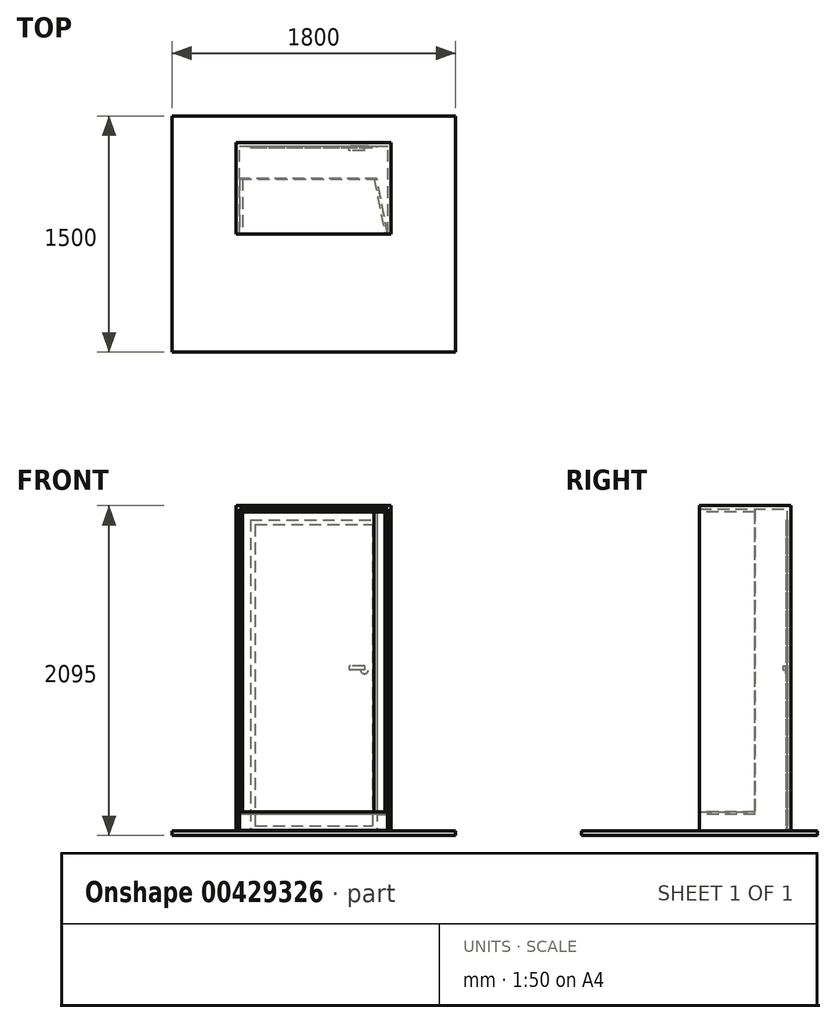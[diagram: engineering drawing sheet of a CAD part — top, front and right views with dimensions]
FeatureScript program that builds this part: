
annotation { "Feature Type Name" : "Feature", "Feature Type Description" : "" }
export const myFeature = defineFeature(function(context is Context, id is Id, definition is map)
    precondition{}
    {
        {
            var Q0;
            Q0=qCreatedBy(makeId("Front.planeOp"),FACE);
            var sketch = newSketch(context, id + "F0", { "sketchPlane" : qUnion([Q0])});
            skLineSegment(sketch, "E0.bottom", {"start": v(-472.5, -1022.5) * mm, "end": v(472.5, -1022.5) * mm});
            skLineSegment(sketch, "E0.top", {"start": v(-472.5, 1022.5) * mm, "end": v(472.5, 1022.5) * mm});
            skLineSegment(sketch, "E0.left", {"start": v(-472.5, -1022.5) * mm, "end": v(-472.5, 1022.5) * mm});
            skLineSegment(sketch, "E0.right", {"start": v(472.5, -1022.5) * mm, "end": v(472.5, 1022.5) * mm});
            skPoint(sketch, "E0.middle", {"position": v(0, 0) * mm});
            skLineSegment(sketch, "E1.0", {"start": v(492.5, -1022.5) * mm, "end": v(492.5, 1042.5) * mm});
            skLineSegment(sketch, "E1.1", {"start": v(-492.5, 1042.5) * mm, "end": v(492.5, 1042.5) * mm});
            skLineSegment(sketch, "E1.2", {"start": v(-492.5, -1022.5) * mm, "end": v(-492.5, 1042.5) * mm});
            skLineSegment(sketch, "E2", {"start": v(-492.5, -1022.5) * mm, "end": v(-472.5, -1022.5) * mm});
            skLineSegment(sketch, "E3", {"start": v(472.5, -1022.5) * mm, "end": v(492.5, -1022.5) * mm});
            skSolve(sketch);
        }
        {
            var Q0;
            Q0=makeQuery(id+"F0.imprint","IMPRINT",FACE,{"disambiguationData":[TD([[makeQuery(id+"F0.imprint","IMPRINT",EDGE,{"derivedFrom":sQuery(id+"F0.wireOp",EDGE,"E0.top")}),1.0]])]});
            extrude(context, id + "F1", {"entities" : qUnion([Q0]), "depth" : 580 * mm});
        }
        {
            var Q0;
            Q0=qCreatedBy(makeId("Front.planeOp"),FACE);
            var sketch = newSketch(context, id + "F2", { "sketchPlane" : qUnion([Q0])});
            skLineSegment(sketch, "E4.bottom", {"start": v(-372.5, 922.5) * mm, "end": v(372.5, 922.5) * mm});
            skLineSegment(sketch, "E4.top", {"start": v(-372.5, -992.5) * mm, "end": v(372.5, -992.5) * mm});
            skLineSegment(sketch, "E4.left", {"start": v(-372.5, 922.5) * mm, "end": v(-372.5, -992.5) * mm});
            skLineSegment(sketch, "E4.right", {"start": v(372.5, 922.5) * mm, "end": v(372.5, -992.5) * mm});
            skLineSegment(sketch, "E5.0", {"start": v(-402.5, 952.5) * mm, "end": v(-402.5, -1022.5) * mm});
            skLineSegment(sketch, "E5.1", {"start": v(-402.5, 952.5) * mm, "end": v(402.5, 952.5) * mm});
            skLineSegment(sketch, "E5.2", {"start": v(402.5, 952.5) * mm, "end": v(402.5, -1022.5) * mm});
            skLineSegment(sketch, "E5.3", {"start": v(-402.5, -1022.5) * mm, "end": v(402.5, -1022.5) * mm});
            skCircle(sketch, "E6", {"center": v(322.5, 0) * mm, "radius": 25 * mm});
            skLineSegment(sketch, "E7.bottom", {"start": v(322.5, 25) * mm, "end": v(232.5, 25) * mm});
            skLineSegment(sketch, "E7.top", {"start": v(322.5, 0) * mm, "end": v(232.5, 0) * mm});
            skLineSegment(sketch, "E7.left", {"start": v(322.5, 25) * mm, "end": v(322.5, 0) * mm});
            skLineSegment(sketch, "E7.right", {"start": v(222.5, 15) * mm, "end": v(222.5, 10) * mm});
            skPoint(sketch, "E8.visualSharp", {"position": v(222.5, 25) * mm});
            skArc(sketch, "E8.filletArc", {"start": v(232.5, 25) * mm, "mid": v(225.43, 22.07) * mm, "end": v(222.5, 15) * mm});
            skPoint(sketch, "E9.visualSharp", {"position": v(222.5, 0) * mm});
            skArc(sketch, "E9.filletArc", {"start": v(222.5, 10) * mm, "mid": v(225.43, 2.93) * mm, "end": v(232.5, 0) * mm});
            skLineSegment(sketch, "E10", {"start": v(-472.5, -1022.5) * mm, "end": v(-402.5, -1022.5) * mm});
            skLineSegment(sketch, "E11", {"start": v(402.5, -1022.5) * mm, "end": v(472.5, -1022.5) * mm});
            skLineSegment(sketch, "E12.bottom", {"start": v(-472.5, -1022.5) * mm, "end": v(472.5, -1022.5) * mm});
            skLineSegment(sketch, "E12.top", {"start": v(-472.5, 1022.5) * mm, "end": v(472.5, 1022.5) * mm});
            skLineSegment(sketch, "E12.left", {"start": v(-472.5, -1022.5) * mm, "end": v(-472.5, 1022.5) * mm});
            skLineSegment(sketch, "E12.right", {"start": v(472.5, -1022.5) * mm, "end": v(472.5, 1022.5) * mm});
            skSolve(sketch);
        }
        {
            var Q0;
            {var subQ1=sQuery(id+"F2.wireOp",EDGE,"E5.0");Q0=makeQuery(id+"F2.imprint","IMPRINT",FACE,{"disambiguationData":[TD([[makeQuery(id+"F2.imprint","IMPRINT",EDGE,{"derivedFrom":subQ1}),-1.0]])]});}
            var Q1;
            Q1=makeQuery(id+"F2.imprint","IMPRINT",FACE,{"disambiguationData":[TD([[makeQuery(id+"F2.imprint","IMPRINT",EDGE,{"derivedFrom":sQuery(id+"F2.wireOp",EDGE,"E4.bottom")}),-1.0]])]});
            extrude(context, id + "F3", {"entities" : qUnion([Q0, Q1]), "depth" : 20 * mm});
        }
        {
            var Q0;
            Q0=makeQuery(id+"F2.imprint","IMPRINT",FACE,{"disambiguationData":[TD([[makeQuery(id+"F2.imprint","IMPRINT",EDGE,{"derivedFrom":sQuery(id+"F2.wireOp",EDGE,"E4.bottom")}),1.0]])]});
            extrude(context, id + "F4", {"entities" : qUnion([Q0]), "operationType" : NewBodyOperationType.ADD, "depth" : 30 * mm});
        }
        {
            var Q0;
            {var subQ0=sQuery(id+"F2.wireOp",EDGE,"E7.left");Q0=makeQuery(id+"F2.imprint","IMPRINT",FACE,{"disambiguationData":[TD([[makeQuery(id+"F2.imprint","IMPRINT",EDGE,{"derivedFrom":subQ0}),1.0]])]});}
            extrude(context, id + "F5", {"entities" : qUnion([Q0]), "operationType" : NewBodyOperationType.ADD, "depth" : 30 * mm});
        }
        {
            var Q0;
            {var subQ4=sQuery(id+"F2.wireOp",EDGE,"E7.bottom");Q0=makeQuery(id+"F2.imprint","IMPRINT",FACE,{"disambiguationData":[TD([[makeQuery(id+"F2.imprint","IMPRINT",EDGE,{"derivedFrom":subQ4}),1.0]])]});}
            var Q1;
            {var subQ0=sQuery(id+"F2.wireOp",EDGE,"E7.left");Q1=makeQuery(id+"F2.imprint","IMPRINT",FACE,{"disambiguationData":[TD([[makeQuery(id+"F2.imprint","IMPRINT",EDGE,{"derivedFrom":subQ0}),-1.0]])]});}
            extrude(context, id + "F6", {"entities" : qUnion([Q0, Q1]), "operationType" : NewBodyOperationType.ADD, "depth" : 50 * mm});
        }
        {
            var Q0;
            Q0=makeQuery(id+"F1.opExtrude","SWEPT_FACE",FACE,{"disambiguationData":[OSD([sQuery(id+"F0.wireOp",EDGE,"E2")])]});
            var sketch = newSketch(context, id + "F7", { "sketchPlane" : qUnion([Q0])});
            skLineSegment(sketch, "E13.bottom", {"start": v(-900, -170) * mm, "end": v(900, -170) * mm});
            skLineSegment(sketch, "E13.top", {"start": v(-900, 1330) * mm, "end": v(900, 1330) * mm});
            skLineSegment(sketch, "E13.left", {"start": v(-900, -170) * mm, "end": v(-900, 1330) * mm});
            skLineSegment(sketch, "E13.right", {"start": v(900, -170) * mm, "end": v(900, 1330) * mm});
            skPoint(sketch, "E13.middle", {"position": v(0, 580) * mm});
            skSolve(sketch);
        }
        {
            var Q0;
            Q0 = qSketchRegion(id + "F7", true);
            extrude(context, id + "F8", {"entities" : qUnion([Q0]), "operationType" : NewBodyOperationType.ADD, "depth" : 30 * mm});
        }
        {
            var Q0;
            Q0=makeQuery(id+"F1.opExtrude","CAP_FACE",FACE,{"disambiguationData":[OSD([sQuery(id+"F0.wireOp",EDGE,"E0.top"),sQuery(id+"F0.wireOp",EDGE,"E0.left"),sQuery(id+"F0.wireOp",EDGE,"E0.right"),sQuery(id+"F0.wireOp",EDGE,"E1.0"),sQuery(id+"F0.wireOp",EDGE,"E1.1"),sQuery(id+"F0.wireOp",EDGE,"E1.2"),sQuery(id+"F0.wireOp",EDGE,"E2"),sQuery(id+"F0.wireOp",EDGE,"E3")])],"isStart":false});
            var sketch = newSketch(context, id + "F9", { "sketchPlane" : qUnion([Q0])});
            skLineSegment(sketch, "E14.bottom", {"start": v(-472.5, 1022.5) * mm, "end": v(472.5, 1022.5) * mm, "construction": true});
            skLineSegment(sketch, "E14.top", {"start": v(-472.5, -1022.5) * mm, "end": v(472.5, -1022.5) * mm, "construction": true});
            skLineSegment(sketch, "E14.left", {"start": v(-472.5, 1022.5) * mm, "end": v(-472.5, -1022.5) * mm, "construction": true});
            skLineSegment(sketch, "E14.right", {"start": v(472.5, 1022.5) * mm, "end": v(472.5, -1022.5) * mm, "construction": true});
            skLineSegment(sketch, "E15.0", {"start": v(470, 1020) * mm, "end": v(470, -1020) * mm});
            skLineSegment(sketch, "E15.1", {"start": v(-470, 1020) * mm, "end": v(470, 1020) * mm});
            skLineSegment(sketch, "E15.2", {"start": v(-470, 1020) * mm, "end": v(-470, -1020) * mm});
            skLineSegment(sketch, "E15.3", {"start": v(-470, -1020) * mm, "end": v(470, -1020) * mm});
            skLineSegment(sketch, "E16.0", {"start": v(-452, 1002) * mm, "end": v(-452, -902) * mm});
            skLineSegment(sketch, "E16.1", {"start": v(-452, 1002) * mm, "end": v(452, 1002) * mm});
            skLineSegment(sketch, "E16.2", {"start": v(452, 1002) * mm, "end": v(452, -902) * mm});
            skLineSegment(sketch, "E17", {"start": v(-452, -920) * mm, "end": v(452, -920) * mm});
            skLineSegment(sketch, "E18", {"start": v(-452, -920) * mm, "end": v(-470, -920) * mm});
            skLineSegment(sketch, "E19", {"start": v(452, -920) * mm, "end": v(470, -920) * mm});
            skLineSegment(sketch, "E20", {"start": v(-452, 1002) * mm, "end": v(-470, 1002) * mm});
            skLineSegment(sketch, "E21", {"start": v(452, 1002) * mm, "end": v(470, 1002) * mm});
            skLineSegment(sketch, "E22.0", {"start": v(-470, -902) * mm, "end": v(470, -902) * mm});
            skSolve(sketch);
        }
        {
            var Q0;
            Q0=makeQuery(id+"F9.imprint","IMPRINT",FACE,{"disambiguationData":[TD([[makeQuery(id+"F9.imprint","IMPRINT",EDGE,{"derivedFrom":sQuery(id+"F9.wireOp",EDGE,"E16.0")}),-1.0]])]});
            extrude(context, id + "F10", {"entities" : qUnion([Q0]), "oppositeDirection" : true, "depth" : 350 * mm});
        }
        {
            var Q0;
            {var subQ1=sQuery(id+"F9.wireOp",EDGE,"E15.1");Q0=makeQuery(id+"F9.imprint","IMPRINT",FACE,{"disambiguationData":[TD([[makeQuery(id+"F9.imprint","IMPRINT",EDGE,{"derivedFrom":subQ1}),-1.0]])]});}
            extrude(context, id + "F11", {"entities" : qUnion([Q0]), "oppositeDirection" : true, "depth" : 350 * mm});
        }
        {
            var Q0;
            Q0=makeQuery(id+"F9.imprint","IMPRINT",FACE,{"disambiguationData":[TD([[makeQuery(id+"F9.imprint","IMPRINT",EDGE,{"derivedFrom":sQuery(id+"F9.wireOp",EDGE,"E17")}),1.0]])]});
            extrude(context, id + "F12", {"entities" : qUnion([Q0]), "oppositeDirection" : true, "depth" : 353 * mm, "hasSecondDirection" : true, "secondDirectionOppositeDirection" : true, "secondDirectionDepth" : 3 * mm});
        }
        {
            var Q0;
            Q0=makeQuery(id+"F9.imprint","IMPRINT",FACE,{"disambiguationData":[TD([[makeQuery(id+"F9.imprint","IMPRINT",EDGE,{"derivedFrom":sQuery(id+"F9.wireOp",EDGE,"E17")}),1.0]])]});
            var Q1;
            {var subQ0=sQuery(id+"F9.wireOp",EDGE,"E15.3");Q1=makeQuery(id+"F9.imprint","IMPRINT",FACE,{"disambiguationData":[TD([[makeQuery(id+"F9.imprint","IMPRINT",EDGE,{"derivedFrom":subQ0}),1.0]])]});}
            extrude(context, id + "F13", {"entities" : qUnion([Q0, Q1]), "oppositeDirection" : true, "depth" : 3 * mm});
        }
        {
            var Q0;
            Q0=makeQuery(id+"F12.opExtrude","SWEPT_FACE",FACE,{"disambiguationData":[OSD([sQuery(id+"F9.wireOp",EDGE,"E22.0")])]});
            var sketch = newSketch(context, id + "F14", { "sketchPlane" : qUnion([Q0])});
            skCircle(sketch, "E23", {"center": v(-470, -580) * mm, "radius": 940 * mm});
            skLineSegment(sketch, "E24", {"start": v(401.2, -227) * mm, "end": v(470, -580) * mm});
            skLineSegment(sketch, "E25", {"start": v(383.2, -227) * mm, "end": v(452, -580) * mm});
            skLineSegment(sketch, "E26", {"start": v(452, -580) * mm, "end": v(470, -580) * mm});
            skLineSegment(sketch, "E27", {"start": v(401.2, -227) * mm, "end": v(383.2, -227) * mm});
            skLineSegment(sketch, "E28.0", {"start": v(401.79, -230) * mm, "end": v(383.79, -230) * mm});
            skSolve(sketch);
        }
        {
            var Q0;
            {var subQ0=sQuery(id+"F14.wireOp",EDGE,"E26");Q0=makeQuery(id+"F14.imprint","IMPRINT",FACE,{"disambiguationData":[TD([[makeQuery(id+"F14.imprint","IMPRINT",EDGE,{"derivedFrom":subQ0}),1.0]])]});}
            var Q1;
            {var subQ0=sQuery(id+"F14.wireOp",EDGE,"E28.0");Q1=makeQuery(id+"F14.imprint","IMPRINT",FACE,{"disambiguationData":[TD([[makeQuery(id+"F14.imprint","IMPRINT",EDGE,{"derivedFrom":subQ0}),1.0]])]});}
            var Q2;
            Q2=makeQuery(id+"F11.opExtrude","SWEPT_FACE",FACE,{"disambiguationData":[OSD([sQuery(id+"F9.wireOp",EDGE,"E16.1"),sQuery(id+"F9.wireOp",EDGE,"E20"),sQuery(id+"F9.wireOp",EDGE,"E21")])]});
            extrude(context, id + "F15", {"entities" : qUnion([Q0, Q1]), "endBound" : BoundingType.UP_TO_SURFACE, "endBoundEntityFace" : qUnion([Q2]), "depth" : 25 * mm});
        }
        {
            var Q0;
            Q0=makeQuery(id+"F12.opExtrude","SWEPT_FACE",FACE,{"disambiguationData":[OSD([sQuery(id+"F9.wireOp",EDGE,"E22.0")])]});
            var sketch = newSketch(context, id + "F16", { "sketchPlane" : qUnion([Q0])});
            skLineSegment(sketch, "E29", {"start": v(470, -227) * mm, "end": v(470, -580) * mm});
            skLineSegment(sketch, "E30", {"start": v(470, -580) * mm, "end": v(470, -580) * mm});
            skLineSegment(sketch, "E31", {"start": v(470, -580) * mm, "end": v(401.2, -227) * mm});
            skLineSegment(sketch, "E32", {"start": v(401.2, -227) * mm, "end": v(470, -227) * mm});
            skSolve(sketch);
        }
        {
            var Q0;
            Q0 = qSketchRegion(id + "F16", true);
            var Q1;
            Q1=makeQuery(id+"F12.opExtrude","SWEPT_FACE",FACE,{"disambiguationData":[OSD([sQuery(id+"F9.wireOp",EDGE,"E17"),sQuery(id+"F9.wireOp",EDGE,"E18"),sQuery(id+"F9.wireOp",EDGE,"E19")])]});
            extrude(context, id + "F17", {"entities" : qUnion([Q0]), "operationType" : NewBodyOperationType.REMOVE, "endBound" : BoundingType.UP_TO_SURFACE, "oppositeDirection" : true, "endBoundEntityFace" : qUnion([Q1]), "depth" : 25 * mm});
        }
        {
            var Q0;
            Q0=makeQuery(id+"F11.opExtrude","SWEPT_FACE",FACE,{"disambiguationData":[OSD([sQuery(id+"F9.wireOp",EDGE,"E16.1"),sQuery(id+"F9.wireOp",EDGE,"E20"),sQuery(id+"F9.wireOp",EDGE,"E21")])]});
            var sketch = newSketch(context, id + "F18", { "sketchPlane" : qUnion([Q0])});
            skLineSegment(sketch, "E33", {"start": v(470, 580) * mm, "end": v(470, 230) * mm});
            skLineSegment(sketch, "E34", {"start": v(470, 230) * mm, "end": v(401.79, 230) * mm});
            skLineSegment(sketch, "E35", {"start": v(401.79, 230) * mm, "end": v(470, 580) * mm});
            skSolve(sketch);
        }
        {
            var Q0;
            Q0 = qSketchRegion(id + "F18", true);
            var Q1;
            Q1=makeQuery(id+"F11.opExtrude","SWEPT_BODY",BODY,{"disambiguationData":[OSD([sQuery(id+"F9.wireOp",EDGE,"E15.0"),sQuery(id+"F9.wireOp",EDGE,"E15.1"),sQuery(id+"F9.wireOp",EDGE,"E15.2"),sQuery(id+"F9.wireOp",EDGE,"E16.1"),sQuery(id+"F9.wireOp",EDGE,"E20"),sQuery(id+"F9.wireOp",EDGE,"E21")])]});
            extrude(context, id + "F19", {"entities" : qUnion([Q0]), "operationType" : NewBodyOperationType.REMOVE, "endBound" : BoundingType.UP_TO_BODY, "oppositeDirection" : true, "endBoundEntityBody" : qUnion([Q1]), "depth" : 25 * mm});
        }
        {
            var Q0;
            Q0=makeQuery(id+"F12.opExtrude","SWEPT_FACE",FACE,{"disambiguationData":[OSD([sQuery(id+"F9.wireOp",EDGE,"E22.0")])]});
            var sketch = newSketch(context, id + "F20", { "sketchPlane" : qUnion([Q0])});
            skLineSegment(sketch, "E36.bottom", {"start": v(-470, -227) * mm, "end": v(401.79, -227) * mm});
            skLineSegment(sketch, "E36.top", {"start": v(-470, -230) * mm, "end": v(401.79, -230) * mm});
            skLineSegment(sketch, "E36.left", {"start": v(-470, -227) * mm, "end": v(-470, -230) * mm});
            skLineSegment(sketch, "E36.right", {"start": v(401.79, -227) * mm, "end": v(401.79, -230) * mm});
            skSolve(sketch);
        }
        {
            var Q0;
            Q0 = qSketchRegion(id + "F20", true);
            var Q1;
            Q1=makeQuery(id+"F11.opExtrude","SWEPT_FACE",FACE,{"disambiguationData":[OSD([sQuery(id+"F9.wireOp",EDGE,"E15.1")])]});
            extrude(context, id + "F21", {"entities" : qUnion([Q0]), "endBound" : BoundingType.UP_TO_SURFACE, "endBoundEntityFace" : qUnion([Q1]), "depth" : 25 * mm});
        }
    });
